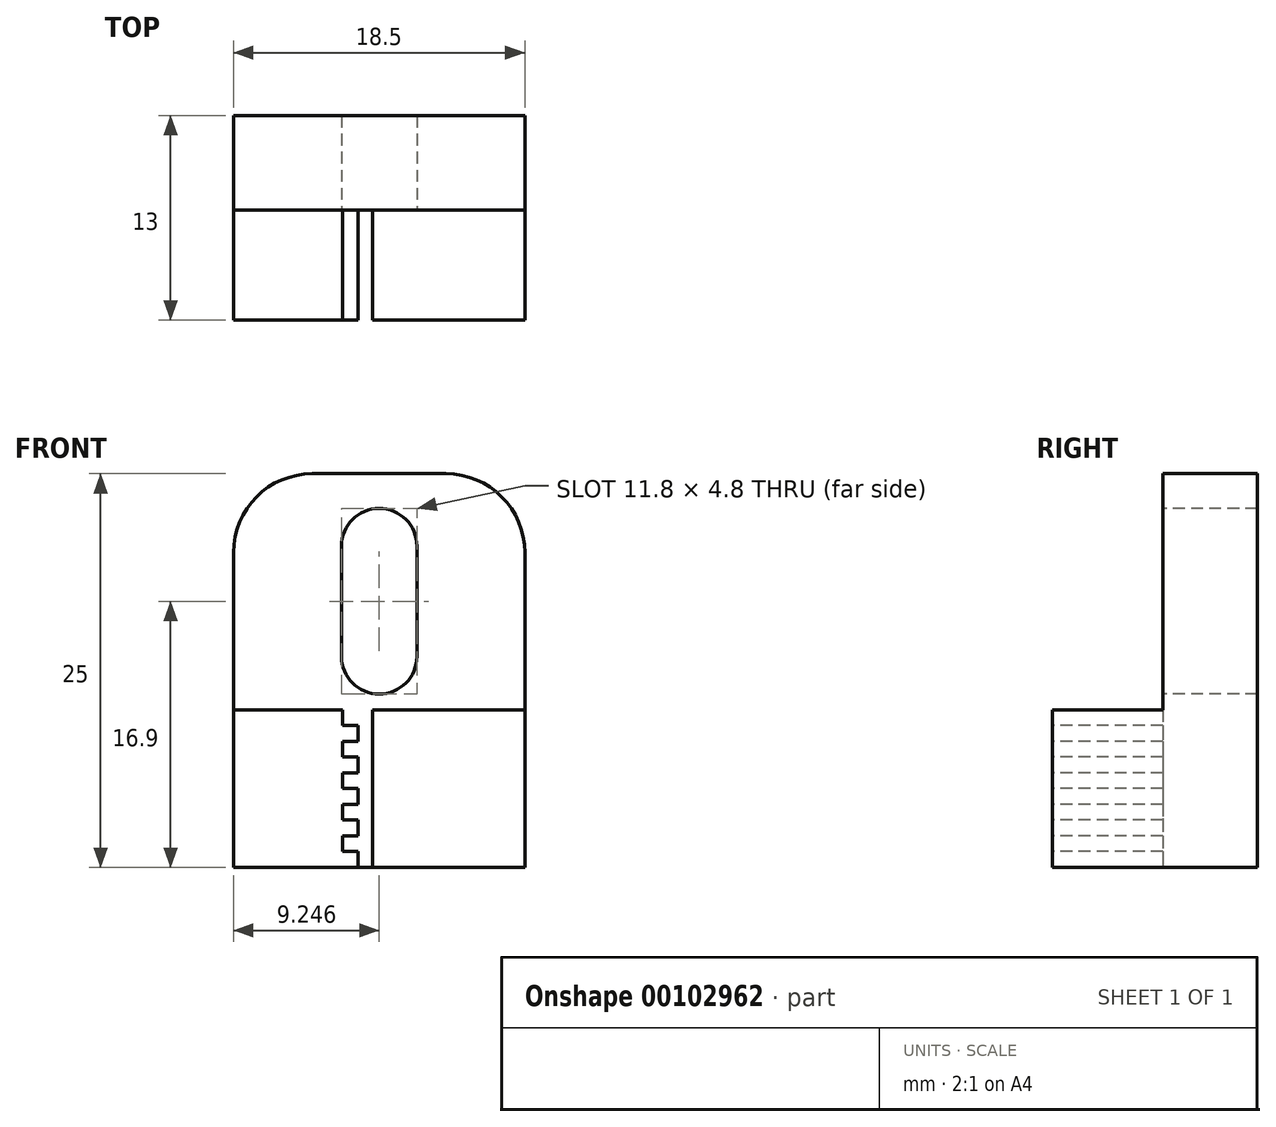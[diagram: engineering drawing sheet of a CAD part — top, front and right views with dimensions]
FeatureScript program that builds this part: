
annotation { "Feature Type Name" : "Feature", "Feature Type Description" : "" }
export const myFeature = defineFeature(function(context is Context, id is Id, definition is map)
    precondition{}
    {
        {
            var Q0;
            Q0=qCreatedBy(makeId("Top.planeOp"),FACE);
            var sketch = newSketch(context, id + "F0", { "sketchPlane" : qUnion([Q0])});
            skLineSegment(sketch, "E0.bottom", {"start": v(-4.96, 0) * mm, "end": v(13.54, 0) * mm});
            skLineSegment(sketch, "E0.top", {"start": v(-4.96, 25) * mm, "end": v(13.54, 25) * mm});
            skLineSegment(sketch, "E0.left", {"start": v(-4.96, 0) * mm, "end": v(-4.96, 25) * mm});
            skLineSegment(sketch, "E0.right", {"start": v(13.54, 0) * mm, "end": v(13.54, 25) * mm});
            skLineSegment(sketch, "E1", {"start": v(-4.96, 5) * mm, "end": v(13.54, 5) * mm});
            skLineSegment(sketch, "E2.bottom", {"start": v(-4.96, 17.95) * mm, "end": v(-1.96, 17.95) * mm});
            skLineSegment(sketch, "E2.top", {"start": v(-4.96, 12.05) * mm, "end": v(-1.96, 12.05) * mm});
            skLineSegment(sketch, "E2.left", {"start": v(-4.96, 17.95) * mm, "end": v(-4.96, 12.05) * mm});
            skLineSegment(sketch, "E2.right", {"start": v(-1.96, 17.95) * mm, "end": v(-1.96, 12.05) * mm});
            skLineSegment(sketch, "E3.bottom", {"start": v(13.54, 17.95) * mm, "end": v(10.54, 17.95) * mm});
            skLineSegment(sketch, "E3.top", {"start": v(13.54, 12.05) * mm, "end": v(10.54, 12.05) * mm});
            skLineSegment(sketch, "E3.left", {"start": v(13.54, 17.95) * mm, "end": v(13.54, 12.05) * mm});
            skLineSegment(sketch, "E3.right", {"start": v(10.54, 17.95) * mm, "end": v(10.54, 12.05) * mm});
            skPoint(sketch, "E4", {"position": v(-1.96, 15) * mm});
            skPoint(sketch, "E5", {"position": v(-4.96, 15) * mm});
            skLineSegment(sketch, "E6", {"start": v(-4.96, 15) * mm, "end": v(13.54, 15) * mm});
            skLineSegment(sketch, "E7", {"start": v(-4.96, 13) * mm, "end": v(13.54, 13) * mm});
            skSolve(sketch);
        }
        {
            var Q0;
            {var subQ0=sQuery(id+"F0.wireOp",EDGE,"E0.bottom");Q0=makeQuery(id+"F0.imprint","IMPRINT",FACE,{"disambiguationData":[TD([[makeQuery(id+"F0.imprint","IMPRINT",EDGE,{"derivedFrom":subQ0}),1.0]])]});}
            var Q1;
            {var subQ1=sQuery(id+"F0.wireOp",EDGE,"E1");Q1=makeQuery(id+"F0.imprint","IMPRINT",FACE,{"disambiguationData":[TD([[makeQuery(id+"F0.imprint","IMPRINT",EDGE,{"derivedFrom":subQ1}),1.0]])]});}
            var Q2;
            {var subQ3=sQuery(id+"F0.wireOp",EDGE,"E2.top");Q2=makeQuery(id+"F0.imprint","IMPRINT",FACE,{"disambiguationData":[TD([[makeQuery(id+"F0.imprint","IMPRINT",EDGE,{"derivedFrom":subQ3}),1.0]])]});}
            var Q3;
            {var subQ3=sQuery(id+"F0.wireOp",EDGE,"E3.top");Q3=makeQuery(id+"F0.imprint","IMPRINT",FACE,{"disambiguationData":[TD([[makeQuery(id+"F0.imprint","IMPRINT",EDGE,{"derivedFrom":subQ3}),-1.0]])]});}
            extrude(context, id + "F1", {"entities" : qUnion([Q0, Q1, Q2, Q3]), "depth" : 10 * mm});
        }
        {
            var Q0;
            Q0=makeQuery(id+"F1.opExtrude","SWEPT_FACE",FACE,{"disambiguationData":[OSD([sQuery(id+"F0.wireOp",EDGE,"E0.bottom")])]});
            var sketch = newSketch(context, id + "F2", { "sketchPlane" : qUnion([Q0])});
            skLineSegment(sketch, "E8", {"start": v(1.96, 10) * mm, "end": v(1.96, 9) * mm});
            skLineSegment(sketch, "E9", {"start": v(1.96, 9) * mm, "end": v(2.96, 9) * mm});
            skLineSegment(sketch, "E10", {"start": v(2.96, 9) * mm, "end": v(2.96, 8) * mm});
            skLineSegment(sketch, "E11", {"start": v(2.96, 8) * mm, "end": v(1.96, 8) * mm});
            skLineSegment(sketch, "E12", {"start": v(1.96, 8) * mm, "end": v(1.96, 7) * mm});
            skLineSegment(sketch, "E13", {"start": v(1.96, 7) * mm, "end": v(2.96, 7) * mm});
            skLineSegment(sketch, "E14", {"start": v(2.96, 7) * mm, "end": v(2.96, 6) * mm});
            skLineSegment(sketch, "E15", {"start": v(2.96, 6) * mm, "end": v(1.96, 6) * mm});
            skLineSegment(sketch, "E16", {"start": v(1.96, 6) * mm, "end": v(1.96, 5) * mm});
            skLineSegment(sketch, "E17", {"start": v(1.96, 5) * mm, "end": v(2.96, 5) * mm});
            skLineSegment(sketch, "E18", {"start": v(2.96, 5) * mm, "end": v(2.96, 4) * mm});
            skLineSegment(sketch, "E19", {"start": v(2.96, 4) * mm, "end": v(1.96, 4) * mm});
            skLineSegment(sketch, "E20", {"start": v(1.96, 4) * mm, "end": v(1.96, 3) * mm});
            skLineSegment(sketch, "E21", {"start": v(1.96, 3) * mm, "end": v(2.96, 3) * mm});
            skLineSegment(sketch, "E22", {"start": v(2.96, 3) * mm, "end": v(2.96, 2) * mm});
            skLineSegment(sketch, "E23", {"start": v(2.96, 2) * mm, "end": v(1.96, 2) * mm});
            skLineSegment(sketch, "E24", {"start": v(1.96, 2) * mm, "end": v(1.96, 1) * mm});
            skLineSegment(sketch, "E25", {"start": v(1.96, 1) * mm, "end": v(2.96, 1) * mm});
            skLineSegment(sketch, "E26", {"start": v(2.96, 1) * mm, "end": v(2.96, 0) * mm});
            skLineSegment(sketch, "E27", {"start": v(2.96, 0) * mm, "end": v(1.96, 0) * mm});
            skLineSegment(sketch, "E28", {"start": v(3.86, 10) * mm, "end": v(3.86, 0) * mm});
            skLineSegment(sketch, "E29", {"start": v(1.96, 10) * mm, "end": v(3.86, 10) * mm});
            skLineSegment(sketch, "E30", {"start": v(3.86, 0) * mm, "end": v(2.96, 0) * mm});
            skSolve(sketch);
        }
        {
            var Q0;
            Q0=makeQuery(id+"F2.imprint","IMPRINT",FACE,{"disambiguationData":[TD([[makeQuery(id+"F2.imprint","IMPRINT",EDGE,{"derivedFrom":sQuery(id+"F2.wireOp",EDGE,"E8")}),1.0]])]});
            extrude(context, id + "F3", {"entities" : qUnion([Q0]), "operationType" : NewBodyOperationType.REMOVE, "oppositeDirection" : true, "depth" : 7 * mm});
        }
        {
            var Q0;
            Q0=makeQuery(id+"F1.opExtrude","CAP_FACE",FACE,{"disambiguationData":[OSD([sQuery(id+"F0.wireOp",EDGE,"E0.bottom"),sQuery(id+"F0.wireOp",EDGE,"E0.left"),sQuery(id+"F0.wireOp",EDGE,"E0.right"),sQuery(id+"F0.wireOp",EDGE,"E7")])],"isStart":false});
            var sketch = newSketch(context, id + "F4", { "sketchPlane" : qUnion([Q0])});
            skLineSegment(sketch, "E31.bottom", {"start": v(-4.96, 0) * mm, "end": v(13.54, 0) * mm});
            skLineSegment(sketch, "E31.top", {"start": v(-4.96, 7) * mm, "end": v(13.54, 7) * mm});
            skLineSegment(sketch, "E31.left", {"start": v(-4.96, 7) * mm, "end": v(-4.96, 0) * mm});
            skLineSegment(sketch, "E31.right", {"start": v(13.54, 7) * mm, "end": v(13.54, 0) * mm});
            skSolve(sketch);
        }
        {
            var Q0;
            {var subQ7=makeQuery(id+"F1.opExtrude","CAP_EDGE",EDGE,{"disambiguationData":[OSD([sQuery(id+"F0.wireOp",EDGE,"E7")])],"isStart":false});Q0=makeQuery(id+"F4.imprint","IMPRINT",FACE,{"disambiguationData":[TD([[makeQuery(id+"F4.imprint","IMPRINT",EDGE,{"derivedFrom":subQ7}),-1.0]])]});}
            extrude(context, id + "F5", {"entities" : qUnion([Q0]), "operationType" : NewBodyOperationType.ADD, "depth" : 15 * mm});
        }
        {
            var Q0;
            Q0=makeQuery(id+"F5.boolean.opBoolean","MERGE",FACE,{"derivedFrom":[makeQuery(id+"F3.boolean.opBoolean","COPY",FACE,{"derivedFrom":makeQuery(id+"F3.opExtrude","CAP_FACE",FACE,{"disambiguationData":[OSD([sQuery(id+"F2.wireOp",EDGE,"E8"),sQuery(id+"F2.wireOp",EDGE,"E9"),sQuery(id+"F2.wireOp",EDGE,"E10"),sQuery(id+"F2.wireOp",EDGE,"E11"),sQuery(id+"F2.wireOp",EDGE,"E12"),sQuery(id+"F2.wireOp",EDGE,"E13"),sQuery(id+"F2.wireOp",EDGE,"E14"),sQuery(id+"F2.wireOp",EDGE,"E15"),sQuery(id+"F2.wireOp",EDGE,"E16"),sQuery(id+"F2.wireOp",EDGE,"E17"),sQuery(id+"F2.wireOp",EDGE,"E18"),sQuery(id+"F2.wireOp",EDGE,"E19"),sQuery(id+"F2.wireOp",EDGE,"E20"),sQuery(id+"F2.wireOp",EDGE,"E21"),sQuery(id+"F2.wireOp",EDGE,"E22"),sQuery(id+"F2.wireOp",EDGE,"E23"),sQuery(id+"F2.wireOp",EDGE,"E24"),sQuery(id+"F2.wireOp",EDGE,"E25"),sQuery(id+"F2.wireOp",EDGE,"E26"),sQuery(id+"F2.wireOp",EDGE,"E28"),sQuery(id+"F2.wireOp",EDGE,"E29"),sQuery(id+"F2.wireOp",EDGE,"E30")])],"isStart":false})}),makeQuery(id+"F5.opExtrude","SWEPT_FACE",FACE,{"disambiguationData":[OSD([sQuery(id+"F4.wireOp",EDGE,"E31.top")])]})]});
            var sketch = newSketch(context, id + "F6", { "sketchPlane" : qUnion([Q0])});
            skArc(sketch, "E32", {"start": v(6.69, 20.4) * mm, "mid": v(4.29, 22.8) * mm, "end": v(1.89, 20.4) * mm});
            skArc(sketch, "E33", {"start": v(1.89, 13.4) * mm, "mid": v(4.29, 11) * mm, "end": v(6.69, 13.4) * mm});
            skLineSegment(sketch, "E34", {"start": v(1.89, 20.4) * mm, "end": v(1.89, 13.4) * mm});
            skLineSegment(sketch, "E35", {"start": v(6.69, 20.4) * mm, "end": v(6.69, 13.4) * mm});
            skPoint(sketch, "E36", {"position": v(4.29, 25) * mm});
            skLineSegment(sketch, "E37", {"start": v(4.29, 10) * mm, "end": v(4.29, 11) * mm});
            skLineSegment(sketch, "E38", {"start": v(4.29, 22.8) * mm, "end": v(4.29, 25) * mm});
            skSolve(sketch);
        }
        {
            var Q0;
            Q0=qSketchRegion(id+"F6",true);
            extrude(context, id + "F7", {"entities" : qUnion([Q0]), "operationType" : NewBodyOperationType.REMOVE, "oppositeDirection" : true, "depth" : 25 * mm});
        }
        {
            var Q0;
            Q0=makeQuery(id+"F5.opExtrude","CAP_EDGE",EDGE,{"disambiguationData":[OSD([sQuery(id+"F0.wireOp",EDGE,"E0.left")])],"isStart":false});
            var Q1;
            Q1=makeQuery(id+"F5.opExtrude","CAP_EDGE",EDGE,{"disambiguationData":[OSD([sQuery(id+"F0.wireOp",EDGE,"E0.right")])],"isStart":false});
            fillet(context, id + "F8", {"entities" : qUnion([Q0, Q1]), "radius" : 5 * mm, "tangentPropagation" : true, "allowEdgeOverflow" : false});
        }
    });
